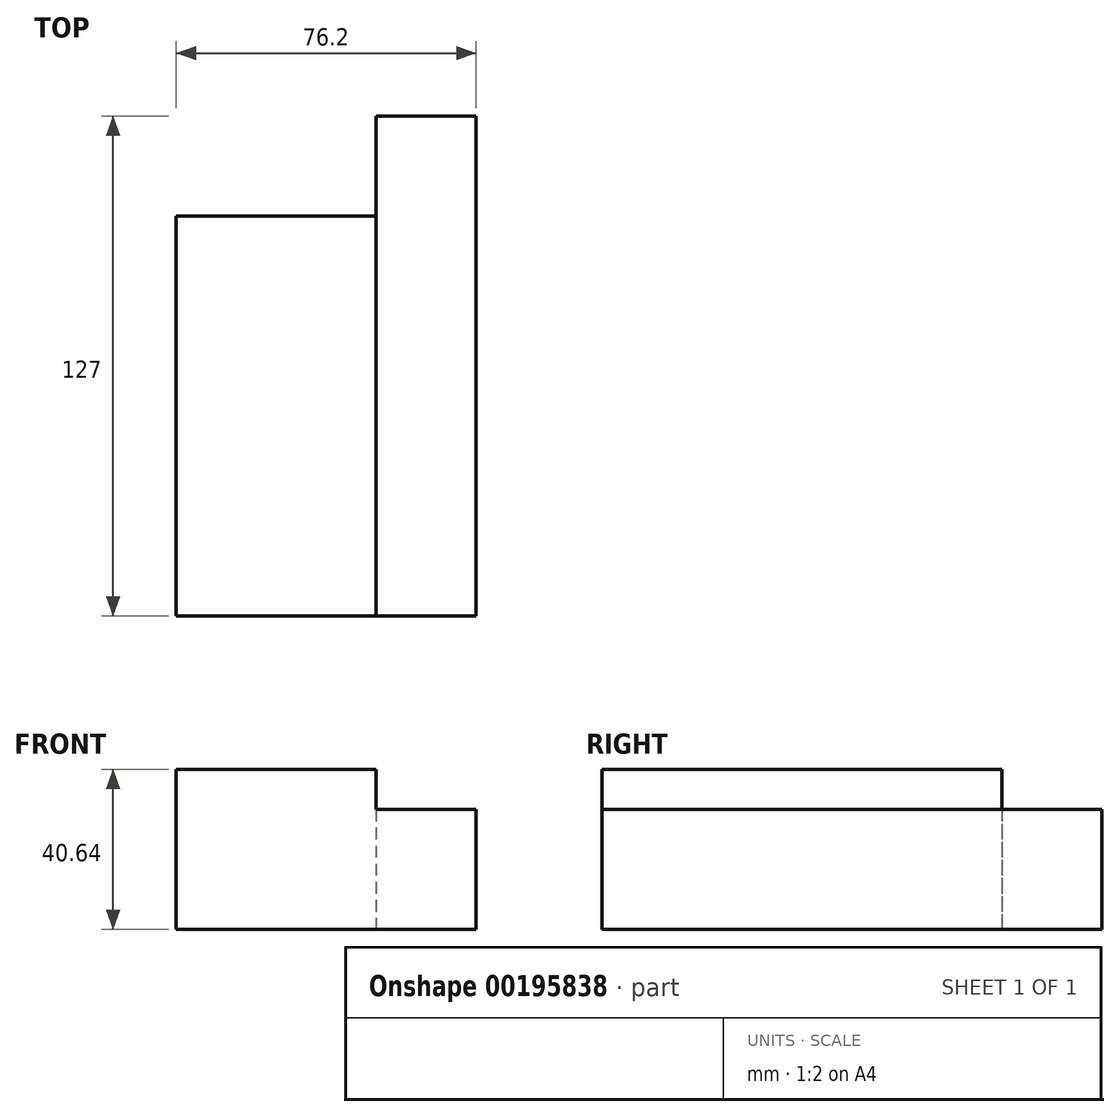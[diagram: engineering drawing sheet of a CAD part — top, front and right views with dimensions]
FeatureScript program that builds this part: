
annotation { "Feature Type Name" : "Feature", "Feature Type Description" : "" }
export const myFeature = defineFeature(function(context is Context, id is Id, definition is map)
    precondition{}
    {
        {
            var Q0;
            Q0=qCreatedBy(makeId("Top.planeOp"),FACE);
            var sketch = newSketch(context, id + "F0", { "sketchPlane" : qUnion([Q0])});
            skLineSegment(sketch, "E0.bottom", {"start": v(-12.7, 63.5) * mm, "end": v(12.7, 63.5) * mm});
            skLineSegment(sketch, "E0.top", {"start": v(-12.7, -63.5) * mm, "end": v(12.7, -63.5) * mm});
            skLineSegment(sketch, "E0.left", {"start": v(-12.7, 63.5) * mm, "end": v(-12.7, -63.5) * mm});
            skLineSegment(sketch, "E0.right", {"start": v(12.7, 63.5) * mm, "end": v(12.7, -63.5) * mm});
            skPoint(sketch, "E0.middle", {"position": v(0, 0) * mm});
            skLineSegment(sketch, "E1.bottom", {"start": v(-63.5, 38.1) * mm, "end": v(-12.7, 38.1) * mm});
            skLineSegment(sketch, "E1.top", {"start": v(-63.5, -63.5) * mm, "end": v(-12.7, -63.5) * mm});
            skLineSegment(sketch, "E1.left", {"start": v(-63.5, 38.1) * mm, "end": v(-63.5, -63.5) * mm});
            skLineSegment(sketch, "E1.right", {"start": v(-12.7, 38.1) * mm, "end": v(-12.7, -63.5) * mm});
            skPoint(sketch, "E1.middle", {"position": v(-38.1, -12.7) * mm});
            skSolve(sketch);
        }
        {
            var Q0;
            Q0=makeQuery(id+"F0.imprint","IMPRINT",FACE,{"disambiguationData":[TD([[makeQuery(id+"F0.imprint","IMPRINT",EDGE,{"derivedFrom":sQuery(id+"F0.wireOp",EDGE,"E0.bottom")}),-1.0]])]});
            extrude(context, id + "F1", {"entities" : qUnion([Q0]), "depth" : 30.48 * mm});
        }
        {
            var Q0;
            Q0=makeQuery(id+"F0.imprint","IMPRINT",FACE,{"disambiguationData":[TD([[makeQuery(id+"F0.imprint","IMPRINT",EDGE,{"derivedFrom":sQuery(id+"F0.wireOp",EDGE,"E1.bottom")}),-1.0]])]});
            extrude(context, id + "F2", {"entities" : qUnion([Q0]), "operationType" : NewBodyOperationType.ADD, "depth" : 40.64 * mm});
        }
    });
